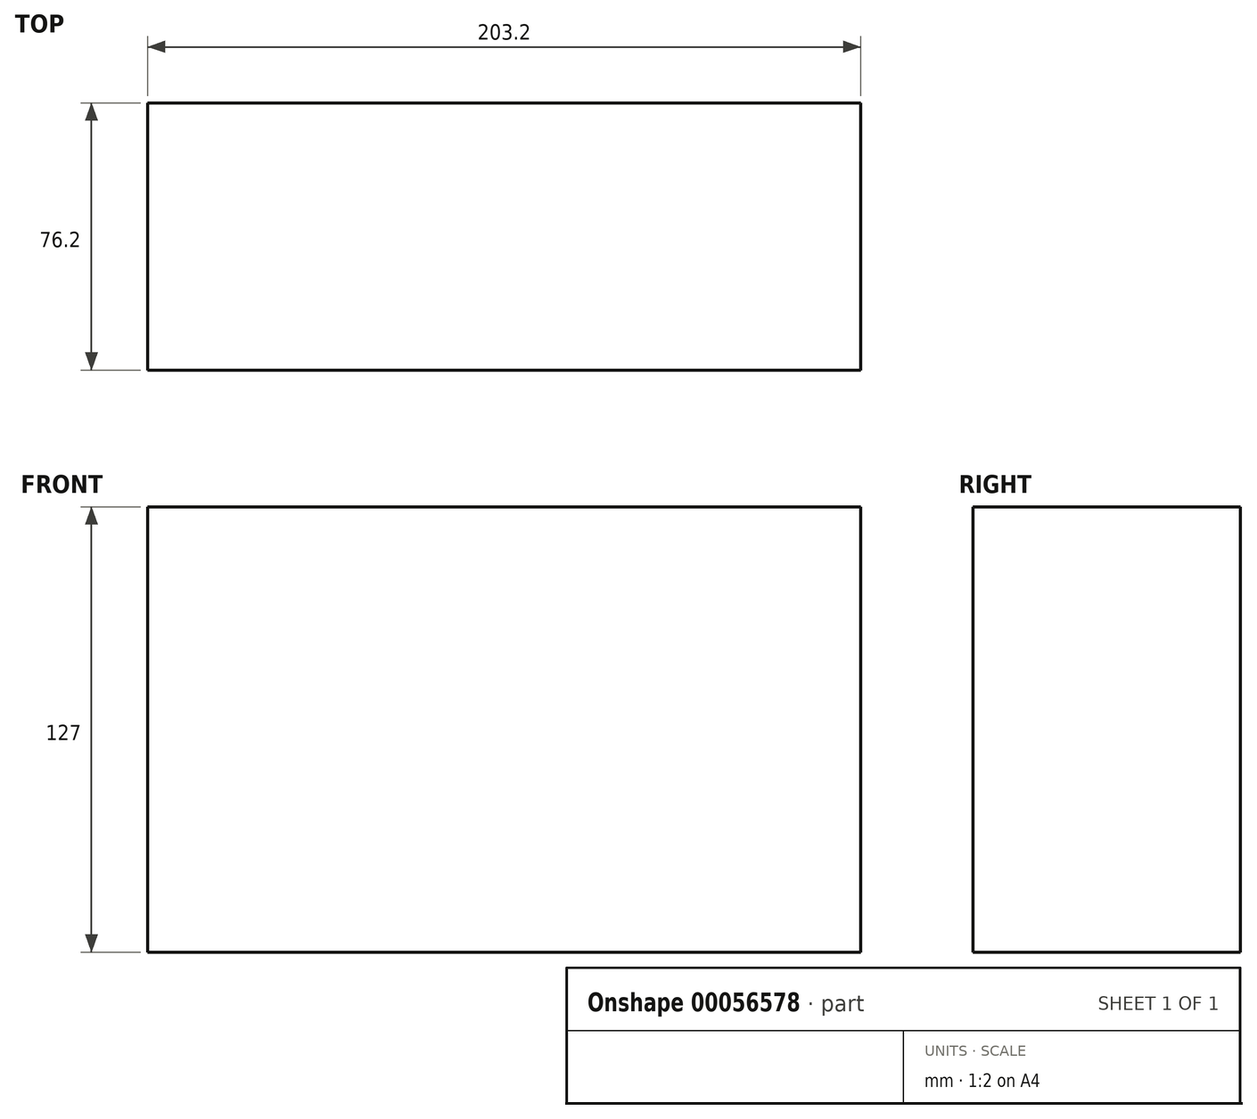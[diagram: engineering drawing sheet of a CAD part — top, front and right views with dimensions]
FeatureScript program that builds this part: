
annotation { "Feature Type Name" : "Feature", "Feature Type Description" : "" }
export const myFeature = defineFeature(function(context is Context, id is Id, definition is map)
    precondition{}
    {
        {
            var Q0;
            Q0=qCreatedBy(makeId("Front.planeOp"),FACE);
            var sketch = newSketch(context, id + "F0", { "sketchPlane" : qUnion([Q0])});
            skLineSegment(sketch, "E0.rect.bottom", {"start": v(101.6, -63.5) * mm, "end": v(-101.6, -63.5) * mm});
            skLineSegment(sketch, "E0.rect.top", {"start": v(101.6, 63.5) * mm, "end": v(-101.6, 63.5) * mm});
            skLineSegment(sketch, "E0.rect.left", {"start": v(101.6, -63.5) * mm, "end": v(101.6, 63.5) * mm});
            skLineSegment(sketch, "E0.rect.right", {"start": v(-101.6, -63.5) * mm, "end": v(-101.6, 63.5) * mm});
            skPoint(sketch, "E0.rect.middle", {"position": v(0, 0) * mm});
            skSolve(sketch);
        }
        {
            var Q0;
            Q0 = qSketchRegion(id + "F0", true);
            extrude(context, id + "F1", {"entities" : qUnion([Q0]), "depth" : 76.2 * mm});
        }
    });
